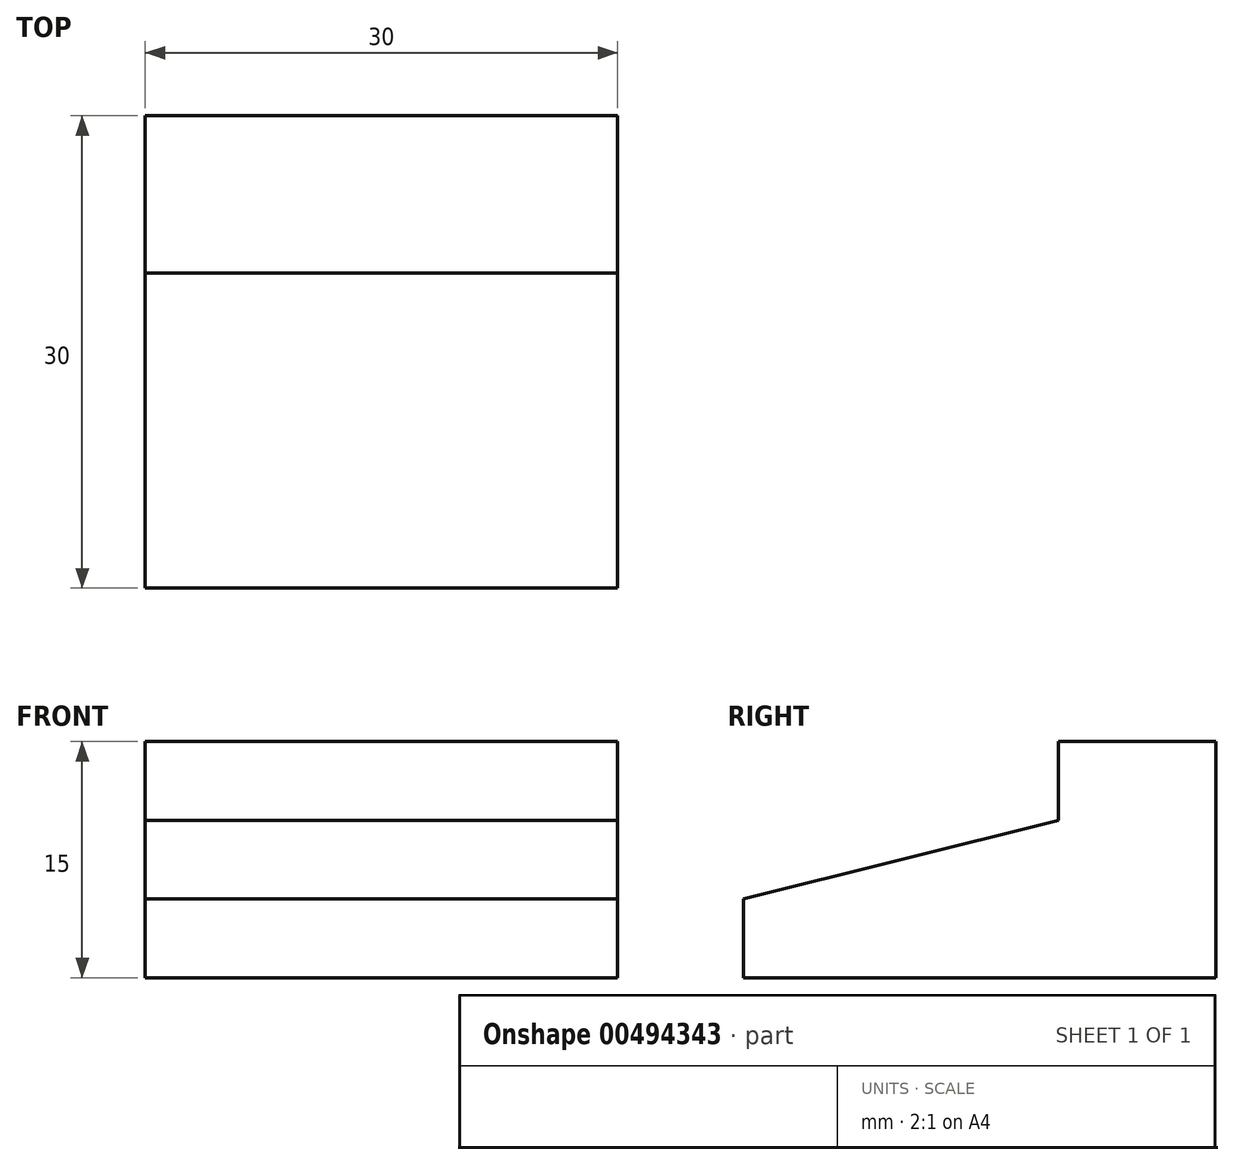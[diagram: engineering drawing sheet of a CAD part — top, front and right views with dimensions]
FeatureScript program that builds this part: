
annotation { "Feature Type Name" : "Feature", "Feature Type Description" : "" }
export const myFeature = defineFeature(function(context is Context, id is Id, definition is map)
    precondition{}
    {
        {
            var Q0;
            Q0=qCreatedBy(makeId("Top.planeOp"),FACE);
            var sketch = newSketch(context, id + "F0", { "sketchPlane" : qUnion([Q0])});
            skLineSegment(sketch, "E0.bottom", {"start": v(-59.75, -45.68) * mm, "end": v(-29.75, -45.68) * mm});
            skLineSegment(sketch, "E0.top", {"start": v(-59.75, -15.68) * mm, "end": v(-29.75, -15.68) * mm});
            skLineSegment(sketch, "E0.left", {"start": v(-59.75, -45.68) * mm, "end": v(-59.75, -15.68) * mm});
            skLineSegment(sketch, "E0.right", {"start": v(-29.75, -45.68) * mm, "end": v(-29.75, -15.68) * mm});
            skSolve(sketch);
        }
        {
            var Q0;
            Q0 = qSketchRegion(id + "F0", true);
            extrude(context, id + "F1", {"entities" : qUnion([Q0]), "depth" : 15 * mm});
        }
        {
            var Q0;
            Q0=makeQuery(id+"F1.opExtrude","SWEPT_FACE",FACE,{"disambiguationData":[OSD([sQuery(id+"F0.wireOp",EDGE,"E0.left")])]});
            var sketch = newSketch(context, id + "F2", { "sketchPlane" : qUnion([Q0])});
            skLineSegment(sketch, "E1", {"start": v(15.68, 15) * mm, "end": v(25.68, 15) * mm});
            skLineSegment(sketch, "E2", {"start": v(25.68, 15) * mm, "end": v(25.68, 10) * mm});
            skLineSegment(sketch, "E3", {"start": v(25.68, 10) * mm, "end": v(45.68, 5) * mm});
            skSolve(sketch);
        }
        {
            var Q0;
            {var subQ0=sQuery(id+"F2.wireOp",EDGE,"E2");Q0=makeQuery(id+"F2.imprint","IMPRINT",FACE,{"disambiguationData":[TD([[makeQuery(id+"F2.imprint","IMPRINT",EDGE,{"derivedFrom":subQ0}),1.0]])]});}
            extrude(context, id + "F3", {"entities" : qUnion([Q0]), "operationType" : NewBodyOperationType.REMOVE, "endBound" : BoundingType.THROUGH_ALL, "oppositeDirection" : true, "depth" : 25 * mm});
        }
    });
